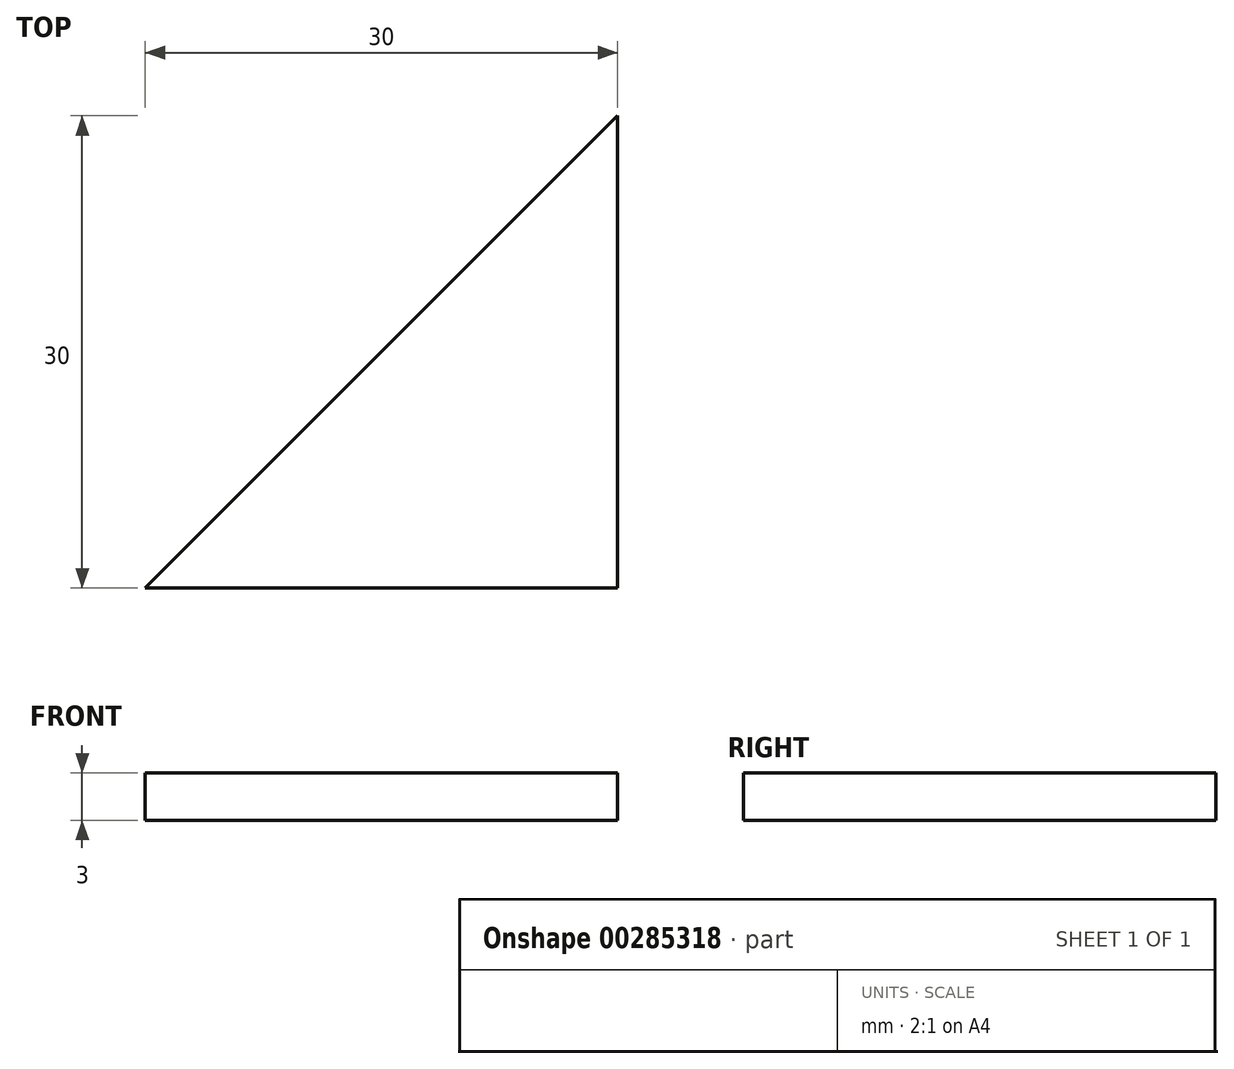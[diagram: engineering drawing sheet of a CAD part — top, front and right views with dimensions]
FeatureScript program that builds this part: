
annotation { "Feature Type Name" : "Feature", "Feature Type Description" : "" }
export const myFeature = defineFeature(function(context is Context, id is Id, definition is map)
    precondition{}
    {
        {
            var Q0;
            Q0=qCreatedBy(makeId("Top.planeOp"),FACE);
            var sketch = newSketch(context, id + "F0", { "sketchPlane" : qUnion([Q0])});
            skLineSegment(sketch, "E0", {"start": v(0, 0) * mm, "end": v(0, 30) * mm});
            skLineSegment(sketch, "E1", {"start": v(0, 30) * mm, "end": v(-30, 0) * mm});
            skLineSegment(sketch, "E2", {"start": v(-30, 0) * mm, "end": v(0, 0) * mm});
            skSolve(sketch);
        }
        {
            var Q0;
            Q0 = qSketchRegion(id + "F0", true);
            extrude(context, id + "F1", {"entities" : qUnion([Q0]), "depth" : 3 * mm});
        }
    });
